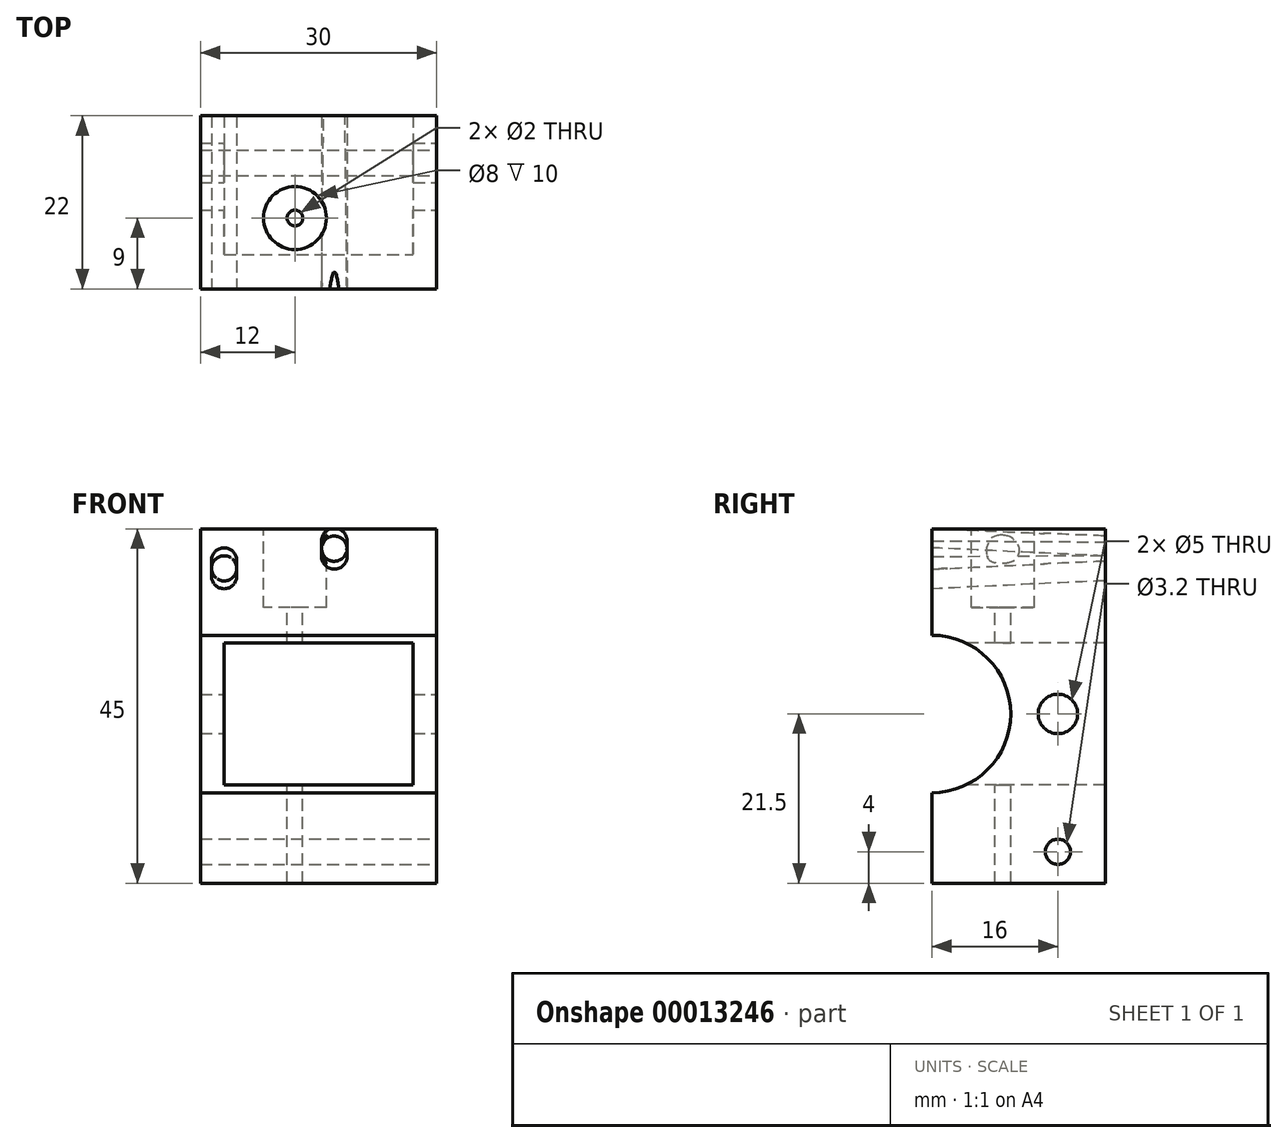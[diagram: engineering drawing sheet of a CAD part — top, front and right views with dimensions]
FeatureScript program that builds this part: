
annotation { "Feature Type Name" : "Feature", "Feature Type Description" : "" }
export const myFeature = defineFeature(function(context is Context, id is Id, definition is map)
    precondition{}
    {
        {
            var Q0;
            Q0=qCreatedBy(makeId("Right.planeOp"),FACE);
            var sketch = newSketch(context, id + "F0", { "sketchPlane" : qUnion([Q0])});
            skLineSegment(sketch, "E0.rect.bottom", {"start": v(11, 22.5) * mm, "end": v(-11, 22.5) * mm});
            skLineSegment(sketch, "E0.rect.top", {"start": v(11, -22.5) * mm, "end": v(-11, -22.5) * mm});
            skLineSegment(sketch, "E0.rect.left", {"start": v(11, 22.5) * mm, "end": v(11, -22.5) * mm});
            skLineSegment(sketch, "E0.rect.right", {"start": v(-11, 22.5) * mm, "end": v(-11, -22.5) * mm});
            skPoint(sketch, "E0.rect.middle", {"position": v(0, 0) * mm});
            skSolve(sketch);
        }
        {
            var Q0;
            Q0 = qSketchRegion(id + "F0", true);
            extrude(context, id + "F1", {"entities" : qUnion([Q0]), "depth" : 30 * mm});
        }
        {
            var Q0;
            Q0=makeQuery(id+"F1.opExtrude","CAP_FACE",FACE,{"disambiguationData":[OSD([sQuery(id+"F0.wireOp",EDGE,"E0.rect.bottom"),sQuery(id+"F0.wireOp",EDGE,"E0.rect.top"),sQuery(id+"F0.wireOp",EDGE,"E0.rect.left"),sQuery(id+"F0.wireOp",EDGE,"E0.rect.right")])],"isStart":false});
            var sketch = newSketch(context, id + "F2", { "sketchPlane" : qUnion([Q0])});
            skCircle(sketch, "E1", {"center": v(5, -18.5) * mm, "radius": 1.6 * mm});
            skSolve(sketch);
        }
        {
            var Q0;
            Q0 = qSketchRegion(id + "F2", true);
            extrude(context, id + "F3", {"entities" : qUnion([Q0]), "operationType" : NewBodyOperationType.REMOVE, "endBound" : BoundingType.THROUGH_ALL, "oppositeDirection" : true, "depth" : 25 * mm});
        }
        {
            var Q0;
            Q0=makeQuery(id+"F1.opExtrude","SWEPT_FACE",FACE,{"disambiguationData":[OSD([sQuery(id+"F0.wireOp",EDGE,"E0.rect.right")])]});
            var sketch = newSketch(context, id + "F4", { "sketchPlane" : qUnion([Q0])});
            skLineSegment(sketch, "E2.bottom", {"start": v(3, -10) * mm, "end": v(27, -10) * mm});
            skLineSegment(sketch, "E2.top", {"start": v(3, 8) * mm, "end": v(27, 8) * mm});
            skLineSegment(sketch, "E2.left", {"start": v(3, -10) * mm, "end": v(3, 8) * mm});
            skLineSegment(sketch, "E2.right", {"start": v(27, -10) * mm, "end": v(27, 8) * mm});
            skSolve(sketch);
        }
        {
            var Q0;
            Q0 = qSketchRegion(id + "F4", true);
            extrude(context, id + "F5", {"entities" : qUnion([Q0]), "operationType" : NewBodyOperationType.REMOVE, "endBound" : BoundingType.THROUGH_ALL, "oppositeDirection" : true, "depth" : 25 * mm});
        }
        {
            var Q0;
            Q0=makeQuery(id+"F1.opExtrude","CAP_FACE",FACE,{"disambiguationData":[OSD([sQuery(id+"F0.wireOp",EDGE,"E0.rect.bottom"),sQuery(id+"F0.wireOp",EDGE,"E0.rect.top"),sQuery(id+"F0.wireOp",EDGE,"E0.rect.left"),sQuery(id+"F0.wireOp",EDGE,"E0.rect.right")])],"isStart":false});
            var sketch = newSketch(context, id + "F6", { "sketchPlane" : qUnion([Q0])});
            skCircle(sketch, "E3", {"center": v(5, -1) * mm, "radius": 2.5 * mm});
            skPoint(sketch, "E4", {"position": v(5, -18.5) * mm});
            skArc(sketch, "E5", {"start": v(-11, -11) * mm, "mid": v(-1, -1) * mm, "end": v(-11, 9) * mm});
            skLineSegment(sketch, "E6", {"start": v(-11, 9) * mm, "end": v(-11, -11) * mm});
            skSolve(sketch);
        }
        {
            var Q0;
            Q0 = qSketchRegion(id + "F6", true);
            extrude(context, id + "F7", {"entities" : qUnion([Q0]), "operationType" : NewBodyOperationType.REMOVE, "endBound" : BoundingType.THROUGH_ALL, "oppositeDirection" : true, "depth" : 25 * mm});
        }
        {
            var Q0;
            Q0=makeQuery(id+"F1.opExtrude","SWEPT_FACE",FACE,{"disambiguationData":[OSD([sQuery(id+"F0.wireOp",EDGE,"E0.rect.bottom")])]});
            var sketch = newSketch(context, id + "F8", { "sketchPlane" : qUnion([Q0])});
            skCircle(sketch, "E7", {"center": v(12, -2) * mm, "radius": 1 * mm});
            skSolve(sketch);
        }
        {
            var Q0;
            Q0 = qSketchRegion(id + "F8", true);
            extrude(context, id + "F9", {"entities" : qUnion([Q0]), "operationType" : NewBodyOperationType.REMOVE, "endBound" : BoundingType.THROUGH_ALL, "oppositeDirection" : true, "depth" : 25 * mm});
        }
        {
            var Q0;
            Q0=makeQuery(id+"F1.opExtrude","SWEPT_FACE",FACE,{"disambiguationData":[OSD([sQuery(id+"F0.wireOp",EDGE,"E0.rect.bottom")])]});
            var sketch = newSketch(context, id + "F10", { "sketchPlane" : qUnion([Q0])});
            skCircle(sketch, "E8", {"center": v(12, -2) * mm, "radius": 4 * mm});
            skSolve(sketch);
        }
        {
            var Q0;
            Q0=makeQuery(id+"F10.imprint","IMPRINT",FACE,{"disambiguationData":[TD([[makeQuery(id+"F10.imprint","IMPRINT",EDGE,{"derivedFrom":sQuery(id+"F10.wireOp",EDGE,"E8")}),1.0]])]});
            extrude(context, id + "F11", {"entities" : qUnion([Q0]), "operationType" : NewBodyOperationType.REMOVE, "oppositeDirection" : true, "depth" : 10 * mm});
        }
        {
            var Q0;
            Q0=makeQuery(id+"F1.opExtrude","SWEPT_FACE",FACE,{"disambiguationData":[OSD([sQuery(id+"F0.wireOp",EDGE,"E0.rect.right")])]});
            var sketch = newSketch(context, id + "F12", { "sketchPlane" : qUnion([Q0])});
            skLineSegment(sketch, "E9", {"start": v(15, 22.5) * mm, "end": v(15, -22.5) * mm, "construction": true});
            skLineSegment(sketch, "E10.bottom", {"start": v(1.4, 18.5) * mm, "end": v(4.6, 18.5) * mm, "construction": true});
            skLineSegment(sketch, "E10.top", {"start": v(1.4, 16.5) * mm, "end": v(4.6, 16.5) * mm, "construction": true});
            skLineSegment(sketch, "E10.left", {"start": v(1.4, 18.5) * mm, "end": v(1.4, 16.5) * mm});
            skLineSegment(sketch, "E10.right", {"start": v(4.6, 18.5) * mm, "end": v(4.6, 16.5) * mm});
            skArc(sketch, "E11", {"start": v(1.4, 18.5) * mm, "mid": v(3, 20.1) * mm, "end": v(4.6, 18.5) * mm});
            skArc(sketch, "E12", {"start": v(1.4, 16.5) * mm, "mid": v(3, 14.9) * mm, "end": v(4.6, 16.5) * mm});
            skSolve(sketch);
        }
        {
            var Q0;
            Q0=makeQuery(id+"F1.opExtrude","SWEPT_FACE",FACE,{"disambiguationData":[OSD([sQuery(id+"F0.wireOp",EDGE,"E0.rect.left")])]});
            var sketch = newSketch(context, id + "F13", { "sketchPlane" : qUnion([Q0])});
            skCircle(sketch, "E13", {"center": v(-3, 17.5) * mm, "radius": 1.6 * mm});
            skLineSegment(sketch, "E14", {"start": v(-15, 22.5) * mm, "end": v(-15, -22.5) * mm, "construction": true});
            skSolve(sketch);
        }
        {
            var Q1;
            Q1 = qSketchRegion(id + "F12", true);
            var Q2;
            Q2 = qSketchRegion(id + "F13", true);
            loft(context, id + "F14", {"operationType" : NewBodyOperationType.REMOVE, "sheetProfilesArray" : [{ "sheetProfileEntities" : qUnion([Q1]) }, { "sheetProfileEntities" : qUnion([Q2]) }]});
        }
        {
            var Q0;
            Q0=makeQuery(id+"F1.opExtrude","SWEPT_FACE",FACE,{"disambiguationData":[OSD([sQuery(id+"F0.wireOp",EDGE,"E0.rect.right")])]});
            var sketch = newSketch(context, id + "F15", { "sketchPlane" : qUnion([Q0])});
            skFitSpline(sketch, "E15.0", {"points": [v(4.6, 19) * mm, v(4.6, 18.82) * mm, v(4.57, 18.64) * mm, v(4.5, 18.47) * mm, v(4.44, 18.27) * mm, v(4.34, 18.1) * mm, v(4.2, 17.94) * mm, v(4.13, 17.86) * mm, v(4.05, 17.79) * mm, v(3.96, 17.72) * mm, v(3.87, 17.65) * mm, v(3.77, 17.6) * mm, v(3.67, 17.55) * mm, v(3.57, 17.5) * mm, v(3.46, 17.46) * mm, v(3.34, 17.44) * mm, v(3.23, 17.41) * mm, v(3.12, 17.4) * mm, v(3, 17.4) * mm, v(2.88, 17.4) * mm, v(2.77, 17.41) * mm, v(2.66, 17.44) * mm, v(2.54, 17.46) * mm, v(2.43, 17.5) * mm, v(2.33, 17.55) * mm, v(2.23, 17.6) * mm, v(2.13, 17.65) * mm, v(2.04, 17.72) * mm, v(1.95, 17.79) * mm, v(1.87, 17.86) * mm, v(1.8, 17.94) * mm, v(1.66, 18.1) * mm, v(1.56, 18.27) * mm, v(1.5, 18.47) * mm, v(1.43, 18.64) * mm, v(1.4, 18.82) * mm, v(1.4, 19) * mm], "construction": true});
            skFitSpline(sketch, "E15.1", {"points": [v(4.6, 21) * mm, v(4.6, 20.33) * mm, v(4.6, 19.67) * mm, v(4.6, 19) * mm], "construction": true});
            skFitSpline(sketch, "E15.2", {"points": [v(1.4, 21) * mm, v(1.4, 21.18) * mm, v(1.43, 21.36) * mm, v(1.5, 21.53) * mm, v(1.56, 21.73) * mm, v(1.66, 21.9) * mm, v(1.8, 22.06) * mm, v(1.87, 22.14) * mm, v(1.95, 22.21) * mm, v(2.04, 22.28) * mm, v(2.13, 22.35) * mm, v(2.23, 22.4) * mm, v(2.33, 22.45) * mm, v(2.43, 22.5) * mm, v(2.54, 22.54) * mm, v(2.66, 22.56) * mm, v(2.77, 22.59) * mm, v(2.88, 22.6) * mm, v(3, 22.6) * mm, v(3.12, 22.6) * mm, v(3.23, 22.59) * mm, v(3.34, 22.56) * mm, v(3.46, 22.54) * mm, v(3.57, 22.5) * mm, v(3.67, 22.45) * mm, v(3.77, 22.4) * mm, v(3.87, 22.35) * mm, v(3.96, 22.28) * mm, v(4.05, 22.21) * mm, v(4.13, 22.14) * mm, v(4.2, 22.06) * mm, v(4.34, 21.9) * mm, v(4.44, 21.73) * mm, v(4.5, 21.53) * mm, v(4.57, 21.36) * mm, v(4.6, 21.18) * mm, v(4.6, 21) * mm], "construction": true});
            skFitSpline(sketch, "E15.3", {"points": [v(1.4, 19) * mm, v(1.4, 19.67) * mm, v(1.4, 20.33) * mm, v(1.4, 21) * mm], "construction": true});
            skLineSegment(sketch, "E16", {"start": v(15, 22.5) * mm, "end": v(15, -22.5) * mm, "construction": true});
            skFitSpline(sketch, "E17.0.MirrorCS", {"points": [v(15.4, 21) * mm, v(15.4, 20.33) * mm, v(15.4, 19.67) * mm, v(15.4, 19) * mm]});
            skFitSpline(sketch, "E17.1.MirrorCS", {"points": [v(15.4, 19) * mm, v(15.4, 18.82) * mm, v(15.43, 18.64) * mm, v(15.5, 18.47) * mm, v(15.56, 18.27) * mm, v(15.66, 18.1) * mm, v(15.8, 17.94) * mm, v(15.87, 17.86) * mm, v(15.95, 17.79) * mm, v(16.04, 17.72) * mm, v(16.13, 17.65) * mm, v(16.23, 17.6) * mm, v(16.33, 17.55) * mm, v(16.43, 17.5) * mm, v(16.54, 17.46) * mm, v(16.66, 17.44) * mm, v(16.77, 17.41) * mm, v(16.88, 17.4) * mm, v(17, 17.4) * mm, v(17.12, 17.4) * mm, v(17.23, 17.41) * mm, v(17.34, 17.44) * mm, v(17.46, 17.46) * mm, v(17.57, 17.5) * mm, v(17.67, 17.55) * mm, v(17.77, 17.6) * mm, v(17.87, 17.65) * mm, v(17.96, 17.72) * mm, v(18.05, 17.79) * mm, v(18.13, 17.86) * mm, v(18.2, 17.94) * mm, v(18.34, 18.1) * mm, v(18.44, 18.27) * mm, v(18.5, 18.47) * mm, v(18.57, 18.64) * mm, v(18.6, 18.82) * mm, v(18.6, 19) * mm]});
            skFitSpline(sketch, "E17.2.MirrorCS", {"points": [v(18.6, 19) * mm, v(18.6, 19.67) * mm, v(18.6, 20.33) * mm, v(18.6, 21) * mm]});
            skFitSpline(sketch, "E17.3.MirrorCS", {"points": [v(18.6, 21) * mm, v(18.6, 21.18) * mm, v(18.57, 21.36) * mm, v(18.5, 21.53) * mm, v(18.44, 21.73) * mm, v(18.34, 21.9) * mm, v(18.2, 22.06) * mm, v(18.13, 22.14) * mm, v(18.05, 22.21) * mm, v(17.96, 22.28) * mm, v(17.87, 22.35) * mm, v(17.77, 22.4) * mm, v(17.67, 22.45) * mm, v(17.57, 22.5) * mm, v(17.46, 22.54) * mm, v(17.34, 22.56) * mm, v(17.23, 22.59) * mm, v(17.12, 22.6) * mm, v(17, 22.6) * mm, v(16.88, 22.6) * mm, v(16.77, 22.59) * mm, v(16.66, 22.56) * mm, v(16.54, 22.54) * mm, v(16.43, 22.5) * mm, v(16.33, 22.45) * mm, v(16.23, 22.4) * mm, v(16.13, 22.35) * mm, v(16.04, 22.28) * mm, v(15.95, 22.21) * mm, v(15.87, 22.14) * mm, v(15.8, 22.06) * mm, v(15.66, 21.9) * mm, v(15.56, 21.73) * mm, v(15.5, 21.53) * mm, v(15.43, 21.36) * mm, v(15.4, 21.18) * mm, v(15.4, 21) * mm]});
            skSolve(sketch);
        }
        {
            var Q0;
            Q0=makeQuery(id+"F1.opExtrude","SWEPT_FACE",FACE,{"disambiguationData":[OSD([sQuery(id+"F0.wireOp",EDGE,"E0.rect.left")])]});
            var sketch = newSketch(context, id + "F16", { "sketchPlane" : qUnion([Q0])});
            skFitSpline(sketch, "E18.0", {"points": [v(-4.36, 19.15) * mm, v(-4.23, 18.96) * mm, v(-4.08, 18.8) * mm, v(-3.88, 18.66) * mm, v(-3.72, 18.56) * mm, v(-3.55, 18.48) * mm, v(-3.36, 18.44) * mm, v(-3.17, 18.4) * mm, v(-2.98, 18.39) * mm, v(-2.8, 18.41) * mm, v(-2.69, 18.43) * mm, v(-2.58, 18.45) * mm, v(-2.48, 18.49) * mm, v(-2.37, 18.53) * mm, v(-2.26, 18.58) * mm, v(-2.15, 18.64) * mm], "construction": true});
            skFitSpline(sketch, "E18.1", {"points": [v(-2.15, 18.64) * mm, v(-2.08, 18.7) * mm, v(-2, 18.75) * mm, v(-1.93, 18.8) * mm, v(-1.86, 18.88) * mm, v(-1.79, 18.95) * mm, v(-1.72, 19.03) * mm, v(-1.66, 19.12) * mm, v(-1.6, 19.21) * mm, v(-1.55, 19.32) * mm, v(-1.5, 19.42) * mm, v(-1.47, 19.53) * mm, v(-1.44, 19.64) * mm, v(-1.42, 19.75) * mm, v(-1.4, 19.86) * mm, v(-1.4, 19.98) * mm, v(-1.4, 20.1) * mm, v(-1.4, 20.2) * mm, v(-1.43, 20.3) * mm, v(-1.45, 20.4) * mm, v(-1.48, 20.5) * mm, v(-1.52, 20.6) * mm, v(-1.55, 20.7) * mm, v(-1.6, 20.77) * mm, v(-1.64, 20.85) * mm], "construction": true});
            skFitSpline(sketch, "E18.2", {"points": [v(-1.64, 20.85) * mm, v(-1.77, 21.04) * mm, v(-1.92, 21.2) * mm, v(-2.12, 21.34) * mm, v(-2.28, 21.44) * mm, v(-2.45, 21.52) * mm, v(-2.64, 21.56) * mm, v(-2.83, 21.6) * mm, v(-3.02, 21.61) * mm, v(-3.2, 21.59) * mm, v(-3.31, 21.57) * mm, v(-3.42, 21.55) * mm, v(-3.52, 21.51) * mm, v(-3.63, 21.47) * mm, v(-3.74, 21.42) * mm, v(-3.85, 21.36) * mm], "construction": true});
            skFitSpline(sketch, "E18.3", {"points": [v(-3.85, 21.36) * mm, v(-3.92, 21.3) * mm, v(-4, 21.25) * mm, v(-4.07, 21.2) * mm, v(-4.14, 21.12) * mm, v(-4.21, 21.05) * mm, v(-4.28, 20.97) * mm, v(-4.34, 20.88) * mm, v(-4.4, 20.79) * mm, v(-4.45, 20.68) * mm, v(-4.5, 20.58) * mm, v(-4.53, 20.47) * mm, v(-4.56, 20.36) * mm, v(-4.58, 20.25) * mm, v(-4.6, 20.14) * mm, v(-4.6, 20.02) * mm, v(-4.6, 19.9) * mm, v(-4.6, 19.8) * mm, v(-4.57, 19.7) * mm, v(-4.55, 19.6) * mm, v(-4.52, 19.5) * mm, v(-4.48, 19.4) * mm, v(-4.45, 19.3) * mm, v(-4.4, 19.23) * mm, v(-4.36, 19.15) * mm], "construction": true});
            skFitSpline(sketch, "E19.0.MirrorCS", {"points": [v(-18.36, 20.85) * mm, v(-18.23, 21.04) * mm, v(-18.08, 21.2) * mm, v(-17.88, 21.34) * mm, v(-17.72, 21.44) * mm, v(-17.55, 21.52) * mm, v(-17.36, 21.56) * mm, v(-17.17, 21.6) * mm, v(-16.98, 21.61) * mm, v(-16.8, 21.59) * mm, v(-16.69, 21.57) * mm, v(-16.58, 21.55) * mm, v(-16.48, 21.51) * mm, v(-16.37, 21.47) * mm, v(-16.26, 21.42) * mm, v(-16.15, 21.36) * mm]});
            skFitSpline(sketch, "E19.1.MirrorCS", {"points": [v(-16.15, 21.36) * mm, v(-16.08, 21.3) * mm, v(-16, 21.25) * mm, v(-15.93, 21.2) * mm, v(-15.86, 21.12) * mm, v(-15.79, 21.05) * mm, v(-15.72, 20.97) * mm, v(-15.66, 20.88) * mm, v(-15.6, 20.79) * mm, v(-15.55, 20.68) * mm, v(-15.5, 20.58) * mm, v(-15.47, 20.47) * mm, v(-15.44, 20.36) * mm, v(-15.42, 20.25) * mm, v(-15.4, 20.14) * mm, v(-15.4, 20.02) * mm, v(-15.4, 19.9) * mm, v(-15.4, 19.8) * mm, v(-15.43, 19.7) * mm, v(-15.45, 19.6) * mm, v(-15.48, 19.5) * mm, v(-15.52, 19.4) * mm, v(-15.55, 19.3) * mm, v(-15.6, 19.23) * mm, v(-15.64, 19.15) * mm]});
            skFitSpline(sketch, "E19.2.MirrorCS", {"points": [v(-15.64, 19.15) * mm, v(-15.77, 18.96) * mm, v(-15.92, 18.8) * mm, v(-16.12, 18.66) * mm, v(-16.28, 18.56) * mm, v(-16.45, 18.48) * mm, v(-16.64, 18.44) * mm, v(-16.83, 18.4) * mm, v(-17.02, 18.39) * mm, v(-17.2, 18.41) * mm, v(-17.31, 18.43) * mm, v(-17.42, 18.45) * mm, v(-17.52, 18.49) * mm, v(-17.63, 18.53) * mm, v(-17.74, 18.58) * mm, v(-17.85, 18.64) * mm]});
            skFitSpline(sketch, "E19.3.MirrorCS", {"points": [v(-17.85, 18.64) * mm, v(-17.92, 18.7) * mm, v(-18, 18.75) * mm, v(-18.07, 18.8) * mm, v(-18.14, 18.88) * mm, v(-18.21, 18.95) * mm, v(-18.28, 19.03) * mm, v(-18.34, 19.12) * mm, v(-18.4, 19.21) * mm, v(-18.45, 19.32) * mm, v(-18.5, 19.42) * mm, v(-18.53, 19.53) * mm, v(-18.56, 19.64) * mm, v(-18.58, 19.75) * mm, v(-18.6, 19.86) * mm, v(-18.6, 19.98) * mm, v(-18.6, 20.1) * mm, v(-18.6, 20.2) * mm, v(-18.57, 20.3) * mm, v(-18.55, 20.4) * mm, v(-18.52, 20.5) * mm, v(-18.48, 20.6) * mm, v(-18.45, 20.7) * mm, v(-18.4, 20.77) * mm, v(-18.36, 20.85) * mm]});
            skSolve(sketch);
        }
        {
            var Q1;
            Q1 = qSketchRegion(id + "F15", true);
            var Q2;
            Q2 = qSketchRegion(id + "F16", true);
            loft(context, id + "F17", {"operationType" : NewBodyOperationType.REMOVE, "sheetProfilesArray" : [{ "sheetProfileEntities" : qUnion([Q1]) }, { "sheetProfileEntities" : qUnion([Q2]) }]});
        }
    });
